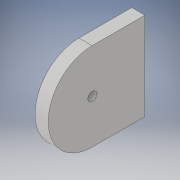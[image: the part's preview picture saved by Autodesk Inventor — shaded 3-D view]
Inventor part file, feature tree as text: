
AUTODESK INVENTOR PART (.ipt)
format: ipt  version: 2019 (Build 230136000, 136)  size: 108,544 bytes
history: native  units: mm
features: sketch x2, other x1, extrude x1, hole x1
ambient origin geometry x8: Origin, YZ Plane, XZ Plane, XY Plane, X Axis, Y Axis, Z Axis, Center Point
bodies: Body1 (feature_tree)
feature tree (5):
  other  "ソリッド1"
  extrude  "押し出し1"  Depth=20.0mm
  hole  "穴1"  [1 undecoded]
  sketch  "スケッチ1"
  sketch  "スケッチ2"
note: 1 required parameter value undecoded (feature->parameter linkage not recoverable at this tier; creation-order binding heuristic only, values carry confidence <= 0.55)
